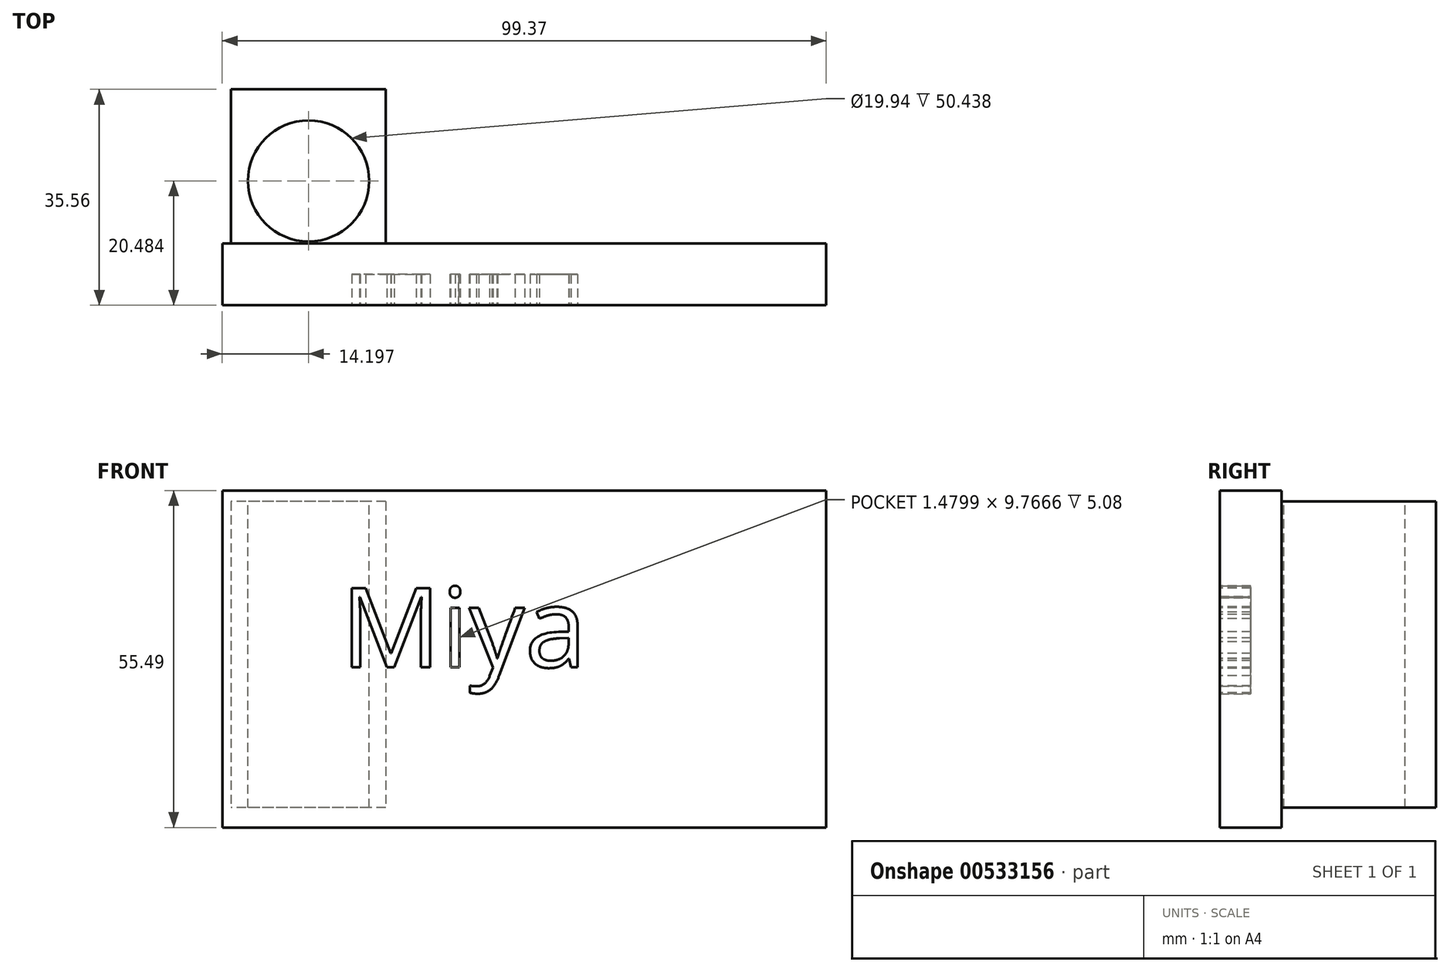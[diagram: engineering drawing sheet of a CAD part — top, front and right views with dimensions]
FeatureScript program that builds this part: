
annotation { "Feature Type Name" : "Feature", "Feature Type Description" : "" }
export const myFeature = defineFeature(function(context is Context, id is Id, definition is map)
    precondition{}
    {
        {
            var Q0;
            Q0=qCreatedBy(makeId("Front.planeOp"),FACE);
            var sketch = newSketch(context, id + "F0", { "sketchPlane" : qUnion([Q0])});
            skLineSegment(sketch, "E0.bottom", {"start": v(-44.8, 33.18) * mm, "end": v(54.57, 33.18) * mm});
            skLineSegment(sketch, "E0.top", {"start": v(-44.8, -22.3) * mm, "end": v(54.57, -22.3) * mm});
            skLineSegment(sketch, "E0.left", {"start": v(-44.8, 33.18) * mm, "end": v(-44.8, -22.3) * mm});
            skLineSegment(sketch, "E0.right", {"start": v(54.57, 33.18) * mm, "end": v(54.57, -22.3) * mm});
            skSolve(sketch);
        }
        {
            var Q0;
            Q0=makeQuery(id+"F0.imprint","IMPRINT",FACE,{"disambiguationData":[TD([[makeQuery(id+"F0.imprint","IMPRINT",EDGE,{"derivedFrom":sQuery(id+"F0.wireOp",EDGE,"E0.bottom")}),-1.0]])]});
            extrude(context, id + "F1", {"entities" : qUnion([Q0]), "depth" : 10.16 * mm, "offsetDistance" : 25.4 * mm});
        }
        {
            var Q0;
            Q0=makeQuery(id+"F1.opExtrude","CAP_FACE",FACE,{"disambiguationData":[OSD([sQuery(id+"F0.wireOp",EDGE,"E0.bottom"),sQuery(id+"F0.wireOp",EDGE,"E0.top"),sQuery(id+"F0.wireOp",EDGE,"E0.left"),sQuery(id+"F0.wireOp",EDGE,"E0.right")])],"isStart":false});
            var sketch = newSketch(context, id + "F2", { "sketchPlane" : qUnion([Q0])});
            skText(sketch, "E1", { "text": "Miya", "fontName": "OpenSans-Regular.ttf"});
            const initialGuessF2  = {"E1": [-0.0253, 0.0041, 1, 0, 0.01314]};
            skSetInitialGuess(sketch, initialGuessF2);
            skSolve(sketch);
        }
        {
            var Q0;
            Q0 = qSketchRegion(id + "F2", true);
            extrude(context, id + "F3", {"entities" : qUnion([Q0]), "operationType" : NewBodyOperationType.REMOVE, "oppositeDirection" : true, "depth" : 5.08 * mm, "offsetDistance" : 25.4 * mm});
        }
        {
            var Q0;
            Q0=makeQuery(id+"F1.opExtrude","CAP_FACE",FACE,{"disambiguationData":[OSD([sQuery(id+"F0.wireOp",EDGE,"E0.bottom"),sQuery(id+"F0.wireOp",EDGE,"E0.top"),sQuery(id+"F0.wireOp",EDGE,"E0.left"),sQuery(id+"F0.wireOp",EDGE,"E0.right")])],"isStart":true});
            var sketch = newSketch(context, id + "F4", { "sketchPlane" : qUnion([Q0])});
            skLineSegment(sketch, "E2.bottom", {"start": v(17.9, 31.38) * mm, "end": v(43.37, 31.38) * mm});
            skLineSegment(sketch, "E2.top", {"start": v(17.9, -19.06) * mm, "end": v(43.37, -19.06) * mm});
            skLineSegment(sketch, "E2.left", {"start": v(17.9, 31.38) * mm, "end": v(17.9, -19.06) * mm});
            skLineSegment(sketch, "E2.right", {"start": v(43.37, 31.38) * mm, "end": v(43.37, -19.06) * mm});
            skSolve(sketch);
        }
        {
            var Q0;
            Q0=makeQuery(id+"F4.imprint","IMPRINT",FACE,{"disambiguationData":[TD([[makeQuery(id+"F4.imprint","IMPRINT",EDGE,{"derivedFrom":sQuery(id+"F4.wireOp",EDGE,"E2.bottom")}),-1.0]])]});
            extrude(context, id + "F5", {"entities" : qUnion([Q0]), "operationType" : NewBodyOperationType.ADD, "depth" : 25.4 * mm, "offsetDistance" : 25.4 * mm});
        }
        {
            var Q0;
            Q0=makeQuery(id+"F5.opExtrude","SWEPT_FACE",FACE,{"disambiguationData":[OSD([sQuery(id+"F4.wireOp",EDGE,"E2.bottom")])]});
            var sketch = newSketch(context, id + "F6", { "sketchPlane" : qUnion([Q0])});
            skCircle(sketch, "E3", {"center": v(-30.6, 10.32) * mm, "radius": 9.97 * mm});
            skSolve(sketch);
        }
        {
            var Q0;
            Q0=makeQuery(id+"F6.imprint","IMPRINT",FACE,{"disambiguationData":[TD([[makeQuery(id+"F6.imprint","IMPRINT",EDGE,{"derivedFrom":sQuery(id+"F6.wireOp",EDGE,"E3")}),1.0]])]});
            extrude(context, id + "F7", {"entities" : qUnion([Q0]), "operationType" : NewBodyOperationType.REMOVE, "endBound" : BoundingType.THROUGH_ALL, "oppositeDirection" : true, "depth" : 25.4 * mm, "offsetDistance" : 25.4 * mm});
        }
    });
